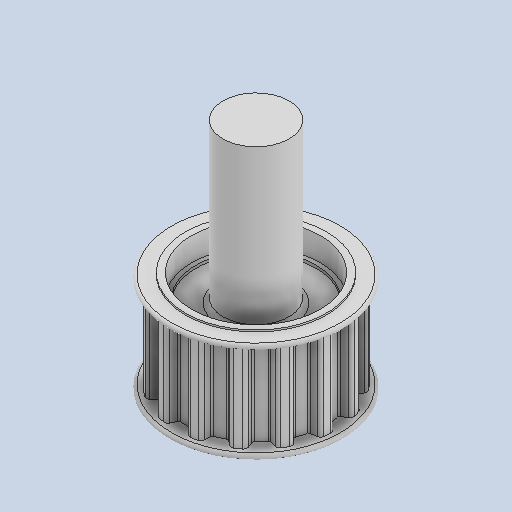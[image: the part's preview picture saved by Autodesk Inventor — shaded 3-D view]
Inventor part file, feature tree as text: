
AUTODESK INVENTOR PART (.ipt)
format: ipt  version: 2022 (Build 260153000, 153)  size: 322,560 bytes
history: native  units: in
note: dims shown in document units (in); Inventor stores cm internally (conversion verified against a paired STEP export)
features: revolve x1
ambient origin geometry x8: Origin, YZ Plane, XZ Plane, XY Plane, X Axis, Y Axis, Z Axis, Center Point
bodies: Solid1 (feature_tree)
feature tree (1):
  revolve  "Revolve1"  [1 undecoded]
note: 1 required parameter value undecoded (feature->parameter linkage not recoverable at this tier; creation-order binding heuristic only, values carry confidence <= 0.55)
